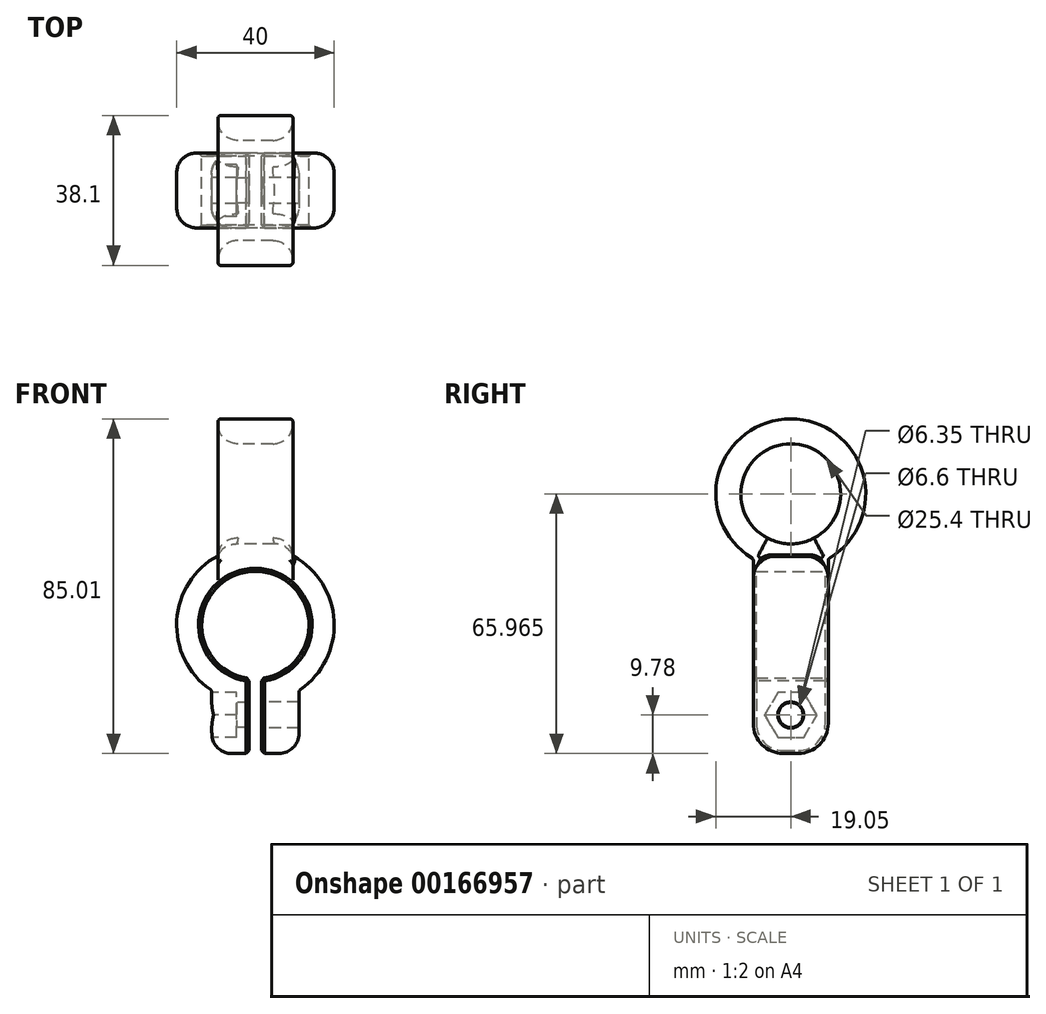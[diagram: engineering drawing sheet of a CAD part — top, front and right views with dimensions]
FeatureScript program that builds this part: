
annotation { "Feature Type Name" : "Feature", "Feature Type Description" : "" }
export const myFeature = defineFeature(function(context is Context, id is Id, definition is map)
    precondition{}
    {
        {
            var Q0;
            Q0=qCreatedBy(makeId("Front.planeOp"),FACE);
            var sketch = newSketch(context, id + "F0", { "sketchPlane" : qUnion([Q0])});
            skArc(sketch, "E0", {"start": v(1.57, -13.56) * mm, "mid": v(0, 13.65) * mm, "end": v(-1.57, -13.56) * mm});
            skArc(sketch, "E1.0", {"start": v(11.1, -16.64) * mm, "mid": v(0, 20) * mm, "end": v(-11.1, -16.64) * mm});
            skLineSegment(sketch, "E2", {"start": v(-1.57, -13.56) * mm, "end": v(-1.57, -19.94) * mm});
            skLineSegment(sketch, "E3.MirrorCS", {"start": v(1.57, -13.56) * mm, "end": v(1.57, -19.94) * mm});
            skLineSegment(sketch, "E4", {"start": v(-1.57, -19.94) * mm, "end": v(-1.57, -32.64) * mm});
            skLineSegment(sketch, "E5", {"start": v(-1.57, -32.64) * mm, "end": v(-11.1, -32.64) * mm});
            skLineSegment(sketch, "E6", {"start": v(-11.1, -32.64) * mm, "end": v(-11.1, -16.64) * mm});
            skLineSegment(sketch, "E7.MirrorCS", {"start": v(1.57, -19.94) * mm, "end": v(1.57, -32.64) * mm});
            skLineSegment(sketch, "E8.MirrorCS", {"start": v(1.57, -32.64) * mm, "end": v(11.1, -32.64) * mm});
            skLineSegment(sketch, "E9.MirrorCS", {"start": v(11.1, -32.64) * mm, "end": v(11.1, -16.64) * mm});
            skSolve(sketch);
        }
        {
            var Q0;
            Q0=makeQuery(id+"F0.imprint","IMPRINT",FACE,{"disambiguationData":[TD([[makeQuery(id+"F0.imprint","IMPRINT",EDGE,{"derivedFrom":sQuery(id+"F0.wireOp",EDGE,"E0")}),-1.0]])]});
            extrude(context, id + "F1", {"entities" : qUnion([Q0]), "endBound" : BoundingType.SYMMETRIC, "depth" : 19.05 * mm});
        }
        {
            var Q0;
            Q0=makeQuery(id+"F1.opExtrude","CAP_EDGE",EDGE,{"disambiguationData":[OSD([sQuery(id+"F0.wireOp",EDGE,"E8.MirrorCS")])],"isStart":true});
            var Q1;
            Q1=makeQuery(id+"F1.opExtrude","CAP_EDGE",EDGE,{"disambiguationData":[OSD([sQuery(id+"F0.wireOp",EDGE,"E5")])],"isStart":true});
            var Q2;
            Q2=makeQuery(id+"F1.opExtrude","CAP_EDGE",EDGE,{"disambiguationData":[OSD([sQuery(id+"F0.wireOp",EDGE,"E8.MirrorCS")])],"isStart":false});
            var Q3;
            Q3=makeQuery(id+"F1.opExtrude","CAP_EDGE",EDGE,{"disambiguationData":[OSD([sQuery(id+"F0.wireOp",EDGE,"E5")])],"isStart":false});
            fillet(context, id + "F2", {"entities" : qUnion([Q0, Q1, Q2, Q3]), "radius" : 7.62 * mm, "tangentPropagation" : true, "allowEdgeOverflow" : false});
        }
        {
            var Q0;
            Q0=makeQuery(id+"F1.opExtrude","CAP_EDGE",EDGE,{"disambiguationData":[OSD([sQuery(id+"F0.wireOp",EDGE,"E0")])],"isStart":false});
            var Q1;
            Q1=makeQuery(id+"F1.opExtrude","CAP_EDGE",EDGE,{"disambiguationData":[OSD([sQuery(id+"F0.wireOp",EDGE,"E0")])],"isStart":true});
            var Q2;
            Q2=makeQuery(id+"F1.opExtrude","CAP_EDGE",EDGE,{"disambiguationData":[OSD([sQuery(id+"F0.wireOp",EDGE,"E2"),sQuery(id+"F0.wireOp",EDGE,"E4")])],"isStart":false});
            var Q3;
            Q3=makeQuery(id+"F1.opExtrude","CAP_EDGE",EDGE,{"disambiguationData":[OSD([sQuery(id+"F0.wireOp",EDGE,"E3.MirrorCS"),sQuery(id+"F0.wireOp",EDGE,"E7.MirrorCS")])],"isStart":false});
            var Q4;
            Q4=makeQuery(id+"F1.opExtrude","CAP_EDGE",EDGE,{"disambiguationData":[OSD([sQuery(id+"F0.wireOp",EDGE,"E3.MirrorCS"),sQuery(id+"F0.wireOp",EDGE,"E7.MirrorCS")])],"isStart":true});
            var Q5;
            Q5=makeQuery(id+"F1.opExtrude","CAP_EDGE",EDGE,{"disambiguationData":[OSD([sQuery(id+"F0.wireOp",EDGE,"E2"),sQuery(id+"F0.wireOp",EDGE,"E4")])],"isStart":true});
            var Q6;
            Q6=makeQuery(id+"F1.opExtrude","SWEPT_EDGE",EDGE,{"disambiguationData":[OSD([sQuery(id+"F0.wireOp",EDGE,"E0"),sQuery(id+"F0.wireOp",EDGE,"E2")])]});
            var Q7;
            Q7=makeQuery(id+"F1.opExtrude","SWEPT_EDGE",EDGE,{"disambiguationData":[OSD([sQuery(id+"F0.wireOp",EDGE,"E0"),sQuery(id+"F0.wireOp",EDGE,"E3.MirrorCS")])]});
            var Q8;
            Q8=makeQuery(id+"F1.opExtrude","SWEPT_EDGE",EDGE,{"disambiguationData":[OSD([sQuery(id+"F0.wireOp",EDGE,"E7.MirrorCS"),sQuery(id+"F0.wireOp",EDGE,"E8.MirrorCS")])]});
            var Q9;
            Q9=makeQuery(id+"F1.opExtrude","SWEPT_EDGE",EDGE,{"disambiguationData":[OSD([sQuery(id+"F0.wireOp",EDGE,"E4"),sQuery(id+"F0.wireOp",EDGE,"E5")])]});
            chamfer(context, id + "F3", {"entities" : qUnion([Q0, Q1, Q2, Q3, Q4, Q5, Q6, Q7, Q8, Q9]), "width" : 0.76 * mm, "tangentPropagation" : true});
        }
        {
            var Q0;
            Q0=makeQuery(id+"F1.opExtrude","SWEPT_EDGE",EDGE,{"disambiguationData":[OSD([sQuery(id+"F0.wireOp",EDGE,"E1.0"),sQuery(id+"F0.wireOp",EDGE,"E9.MirrorCS")])]});
            var Q1;
            Q1=makeQuery(id+"F1.opExtrude","SWEPT_EDGE",EDGE,{"disambiguationData":[OSD([sQuery(id+"F0.wireOp",EDGE,"E1.0"),sQuery(id+"F0.wireOp",EDGE,"E6")])]});
            fillet(context, id + "F4", {"entities" : qUnion([Q0, Q1]), "radius" : 0.79 * mm, "tangentPropagation" : true, "allowEdgeOverflow" : false});
        }
        {
            var Q0;
            Q0=makeQuery(id+"F1.opExtrude","SWEPT_FACE",FACE,{"disambiguationData":[OSD([sQuery(id+"F0.wireOp",EDGE,"E6")])]});
            var sketch = newSketch(context, id + "F5", { "sketchPlane" : qUnion([Q0])});
            skCircle(sketch, "E10", {"center": v(0, -22.86) * mm, "radius": 3.18 * mm});
            skSolve(sketch);
        }
        {
            var Q0;
            Q0=makeQuery(id+"F5.imprint","IMPRINT",FACE,{"disambiguationData":[TD([[makeQuery(id+"F5.imprint","IMPRINT",EDGE,{"derivedFrom":sQuery(id+"F5.wireOp",EDGE,"E10")}),1.0]])]});
            extrude(context, id + "F6", {"entities" : qUnion([Q0]), "operationType" : NewBodyOperationType.REMOVE, "endBound" : BoundingType.UP_TO_NEXT, "oppositeDirection" : true, "depth" : 25.4 * mm});
        }
        {
            var Q0;
            Q0=makeQuery(id+"F1.opExtrude","SWEPT_FACE",FACE,{"disambiguationData":[OSD([sQuery(id+"F0.wireOp",EDGE,"E3.MirrorCS"),sQuery(id+"F0.wireOp",EDGE,"E7.MirrorCS")])]});
            var sketch = newSketch(context, id + "F7", { "sketchPlane" : qUnion([Q0])});
            skCircle(sketch, "E11.0", {"center": v(0, -22.86) * mm, "radius": 3.18 * mm});
            skCircle(sketch, "E12", {"center": v(0, -22.86) * mm, "radius": 3.3 * mm});
            skSolve(sketch);
        }
        {
            var Q0;
            Q0=makeQuery(id+"F7.imprint","IMPRINT",FACE,{"disambiguationData":[TD([[makeQuery(id+"F7.imprint","IMPRINT",EDGE,{"derivedFrom":sQuery(id+"F7.wireOp",EDGE,"E11.0")}),1.0]])]});
            var Q1;
            Q1=makeQuery(id+"F7.imprint","IMPRINT",FACE,{"disambiguationData":[TD([[makeQuery(id+"F7.imprint","IMPRINT",EDGE,{"derivedFrom":sQuery(id+"F7.wireOp",EDGE,"E11.0")}),-1.0]])]});
            extrude(context, id + "F8", {"entities" : qUnion([Q0, Q1]), "operationType" : NewBodyOperationType.REMOVE, "endBound" : BoundingType.UP_TO_NEXT, "oppositeDirection" : true, "depth" : 25.4 * mm});
        }
        {
            var Q0;
            Q0=qCreatedBy(makeId("Right.planeOp"),FACE);
            var sketch = newSketch(context, id + "F9", { "sketchPlane" : qUnion([Q0])});
            skCircle(sketch, "E13", {"center": v(0, 33.32) * mm, "radius": 12.7 * mm});
            skCircle(sketch, "E14.0", {"center": v(0, 33.32) * mm, "radius": 19.05 * mm});
            skSolve(sketch);
        }
        {
            var Q0;
            Q0=makeQuery(id+"F9.imprint","IMPRINT",FACE,{"disambiguationData":[TD([[makeQuery(id+"F9.imprint","IMPRINT",EDGE,{"derivedFrom":sQuery(id+"F9.wireOp",EDGE,"E13")}),-1.0]])]});
            extrude(context, id + "F10", {"entities" : qUnion([Q0]), "operationType" : NewBodyOperationType.ADD, "endBound" : BoundingType.SYMMETRIC, "depth" : 19.05 * mm});
        }
        {
            var Q0;
            Q0=makeQuery(id+"F10.opExtrude","CAP_EDGE",EDGE,{"disambiguationData":[OSD([sQuery(id+"F9.wireOp",EDGE,"E13")])],"isStart":false});
            var Q1;
            Q1=makeQuery(id+"F10.opExtrude","CAP_EDGE",EDGE,{"disambiguationData":[OSD([sQuery(id+"F9.wireOp",EDGE,"E13")])],"isStart":true});
            fillet(context, id + "F11", {"entities" : qUnion([Q0, Q1]), "radius" : 5.08 * mm, "tangentPropagation" : true, "allowEdgeOverflow" : false});
        }
        {
            var Q0;
            {var subQ0=sQuery(id+"F0.wireOp",EDGE,"E6");var subQ1=sQuery(id+"F0.wireOp",EDGE,"E1.0");Q0=makeQuery(id+"F10.boolean.opBoolean","SPLIT",EDGE,{"disambiguationData":[TD([makeQuery(id+"F4.opFillet","BLEND_FACE",FACE,{"disambiguationData":[OSD([subQ1,subQ0])]})])],"derivedFrom":makeQuery(id+"F1.opExtrude","CAP_EDGE",EDGE,{"disambiguationData":[OSD([subQ1])],"isStart":false})});}
            var Q1;
            {var subQ0=sQuery(id+"F0.wireOp",EDGE,"E9.MirrorCS");var subQ1=sQuery(id+"F0.wireOp",EDGE,"E1.0");Q1=makeQuery(id+"F10.boolean.opBoolean","SPLIT",EDGE,{"disambiguationData":[TD([makeQuery(id+"F4.opFillet","BLEND_FACE",FACE,{"disambiguationData":[OSD([subQ1,subQ0])]})])],"derivedFrom":makeQuery(id+"F1.opExtrude","CAP_EDGE",EDGE,{"disambiguationData":[OSD([subQ1])],"isStart":false})});}
            fillet(context, id + "F12", {"entities" : qUnion([Q0, Q1]), "radius" : 5.08 * mm, "tangentPropagation" : true, "allowEdgeOverflow" : false});
        }
        {
            var Q0;
            Q0=makeQuery(id+"F10.opExtrude","CAP_EDGE",EDGE,{"disambiguationData":[OSD([sQuery(id+"F9.wireOp",EDGE,"E14.0")])],"isStart":true});
            var Q1;
            Q1=makeQuery(id+"F10.opExtrude","CAP_EDGE",EDGE,{"disambiguationData":[OSD([sQuery(id+"F9.wireOp",EDGE,"E14.0")])],"isStart":false});
            var Q2;
            Q2=makeQuery(id+"F10.boolean.opBoolean","INTERSECT",EDGE,{"derivedFrom":[makeQuery(id+"F1.opExtrude","CAP_FACE",FACE,{"disambiguationData":[OSD([sQuery(id+"F0.wireOp",EDGE,"E0"),sQuery(id+"F0.wireOp",EDGE,"E1.0"),sQuery(id+"F0.wireOp",EDGE,"E2"),sQuery(id+"F0.wireOp",EDGE,"E3.MirrorCS"),sQuery(id+"F0.wireOp",EDGE,"E4"),sQuery(id+"F0.wireOp",EDGE,"E5"),sQuery(id+"F0.wireOp",EDGE,"E6"),sQuery(id+"F0.wireOp",EDGE,"E7.MirrorCS"),sQuery(id+"F0.wireOp",EDGE,"E8.MirrorCS"),sQuery(id+"F0.wireOp",EDGE,"E9.MirrorCS")])],"isStart":false}),makeQuery(id+"F10.opExtrude","SWEPT_FACE",FACE,{"disambiguationData":[OSD([sQuery(id+"F9.wireOp",EDGE,"E14.0")])]})]});
            var Q3;
            Q3=makeQuery(id+"F10.boolean.opBoolean","INTERSECT",EDGE,{"derivedFrom":[makeQuery(id+"F1.opExtrude","CAP_FACE",FACE,{"disambiguationData":[OSD([sQuery(id+"F0.wireOp",EDGE,"E0"),sQuery(id+"F0.wireOp",EDGE,"E1.0"),sQuery(id+"F0.wireOp",EDGE,"E2"),sQuery(id+"F0.wireOp",EDGE,"E3.MirrorCS"),sQuery(id+"F0.wireOp",EDGE,"E4"),sQuery(id+"F0.wireOp",EDGE,"E5"),sQuery(id+"F0.wireOp",EDGE,"E6"),sQuery(id+"F0.wireOp",EDGE,"E7.MirrorCS"),sQuery(id+"F0.wireOp",EDGE,"E8.MirrorCS"),sQuery(id+"F0.wireOp",EDGE,"E9.MirrorCS")])],"isStart":true}),makeQuery(id+"F10.opExtrude","SWEPT_FACE",FACE,{"disambiguationData":[OSD([sQuery(id+"F9.wireOp",EDGE,"E14.0")])]})]});
            var Q4;
            {var subQ1=sQuery(id+"F9.wireOp",EDGE,"E13");var subQ2=sQuery(id+"F0.wireOp",EDGE,"E9.MirrorCS");var subQ10=sQuery(id+"F0.wireOp",EDGE,"E1.0");Q4=makeQuery(id+"F11.opFillet","BLEND_EDGE",EDGE,{"blendedFrom":[makeQuery(id+"F10.opExtrude","CAP_EDGE",EDGE,{"disambiguationData":[OSD([subQ1])],"isStart":false}),makeQuery(id+"F10.boolean.opBoolean","SPLIT",FACE,{"disambiguationData":[TD([makeQuery(id+"F4.opFillet","BLEND_FACE",FACE,{"disambiguationData":[OSD([subQ10,subQ2])]})])],"derivedFrom":makeQuery(id+"F1.opExtrude","SWEPT_FACE",FACE,{"disambiguationData":[OSD([subQ10])]})})],"blendedInto":[makeQuery(id+"F10.boolean.opBoolean","SPLIT",FACE,{"disambiguationData":[TD([makeQuery(id+"F4.opFillet","BLEND_FACE",FACE,{"disambiguationData":[OSD([subQ10,subQ2])]})])],"derivedFrom":makeQuery(id+"F1.opExtrude","SWEPT_FACE",FACE,{"disambiguationData":[OSD([subQ10])]})})]});}
            fillet(context, id + "F13", {"entities" : qUnion([Q0, Q1, Q2, Q3, Q4]), "radius" : 0.76 * mm, "tangentPropagation" : true, "allowEdgeOverflow" : false});
        }
        {
            var Q0;
            Q0=makeQuery(id+"F1.opExtrude","SWEPT_FACE",FACE,{"disambiguationData":[OSD([sQuery(id+"F0.wireOp",EDGE,"E6")])]});
            var sketch = newSketch(context, id + "F14", { "sketchPlane" : qUnion([Q0])});
            skCircle(sketch, "E15.cCircle", {"center": v(0, -22.86) * mm, "radius": 5.72 * mm, "construction": true});
            skPoint(sketch, "E15.cCircle.perimeterSnap0", {"position": v(0, -27.56) * mm});
            skLineSegment(sketch, "E15.0", {"start": v(3.3, -28.58) * mm, "end": v(-3.3, -28.58) * mm});
            skLineSegment(sketch, "E15.1", {"start": v(-3.3, -28.57) * mm, "end": v(-6.6, -22.86) * mm});
            skLineSegment(sketch, "E15.2", {"start": v(-6.6, -22.86) * mm, "end": v(-3.3, -17.14) * mm});
            skLineSegment(sketch, "E15.3", {"start": v(-3.3, -17.14) * mm, "end": v(3.3, -17.14) * mm});
            skLineSegment(sketch, "E15.4", {"start": v(3.3, -17.15) * mm, "end": v(6.6, -22.86) * mm});
            skLineSegment(sketch, "E15.5", {"start": v(6.6, -22.86) * mm, "end": v(3.3, -28.57) * mm});
            skPoint(sketch, "E15.0.midPoint", {"position": v(0, -28.58) * mm});
            skPoint(sketch, "E15.0.midPoint.positionSnap0", {"position": v(0, -27.56) * mm});
            skSolve(sketch);
        }
        {
            var Q0;
            {var subQ0=sQuery(id+"F14.wireOp",EDGE,"E15.3");Q0=makeQuery(id+"F14.imprint","IMPRINT",FACE,{"disambiguationData":[TD([[makeQuery(id+"F14.imprint","IMPRINT",EDGE,{"derivedFrom":subQ0}),-1.0]])]});}
            var Q1;
            Q1=makeQuery(id+"F14.imprint","IMPRINT",FACE,{"disambiguationData":[TD([[makeQuery(id+"F14.imprint","IMPRINT",EDGE,{"derivedFrom":sQuery(id+"F14.wireOp",EDGE,"E15.0")}),-1.0]])]});
            extrude(context, id + "F15", {"entities" : qUnion([Q0, Q1]), "operationType" : NewBodyOperationType.REMOVE, "oppositeDirection" : true, "depth" : 6.35 * mm});
        }
    });
